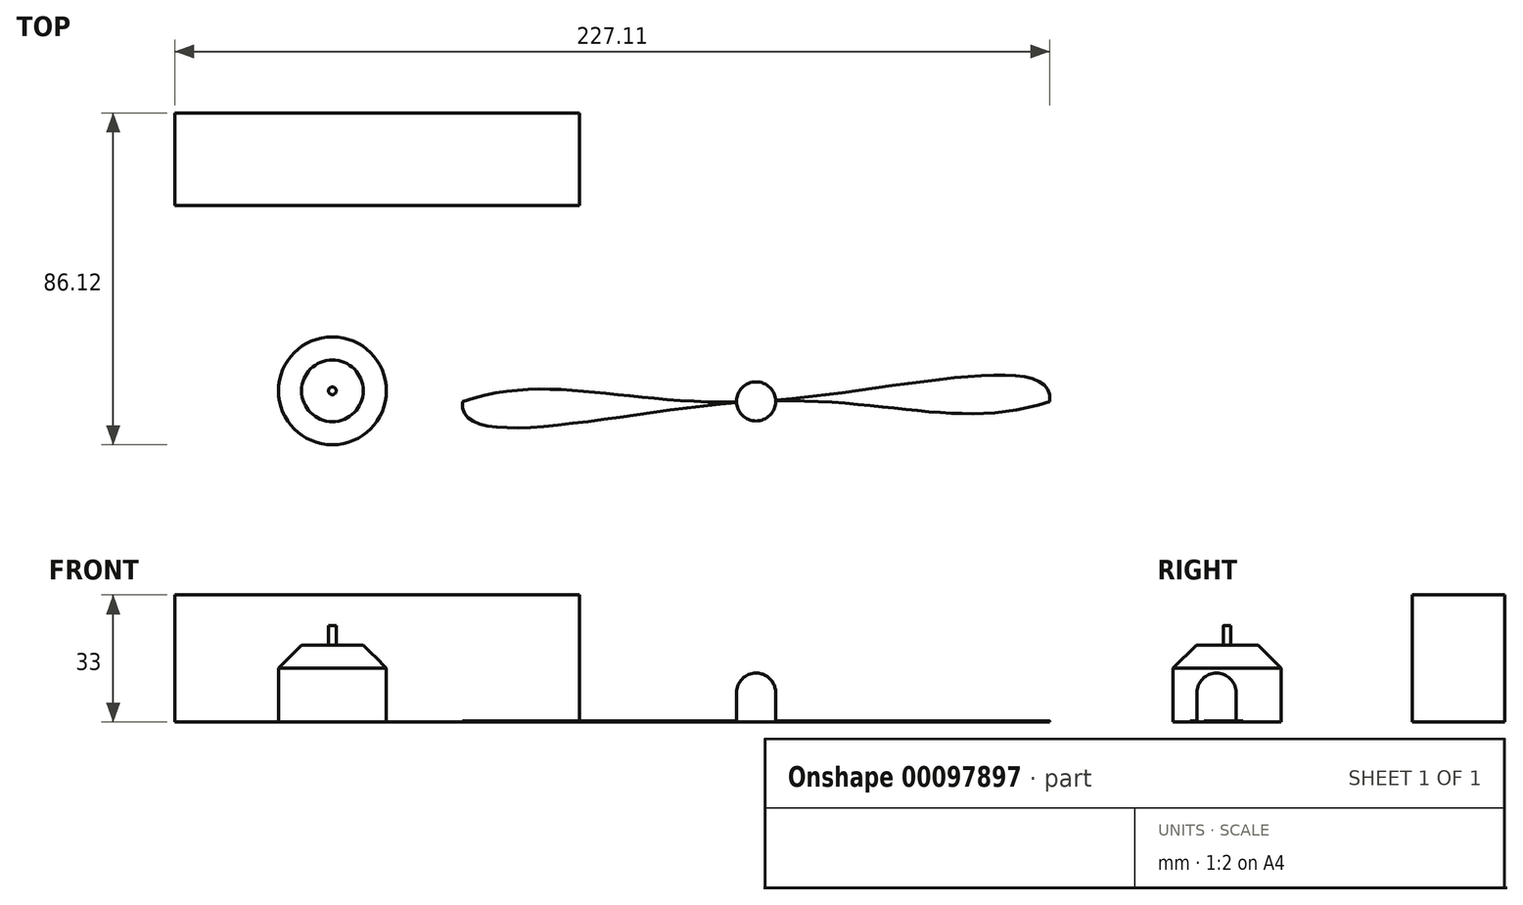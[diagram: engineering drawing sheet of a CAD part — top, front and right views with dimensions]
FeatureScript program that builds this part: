
annotation { "Feature Type Name" : "Feature", "Feature Type Description" : "" }
export const myFeature = defineFeature(function(context is Context, id is Id, definition is map)
    precondition{}
    {
        {
            var Q0;
            Q0=qCreatedBy(makeId("Top.planeOp"),FACE);
            var sketch = newSketch(context, id + "F0", { "sketchPlane" : qUnion([Q0])});
            skLineSegment(sketch, "E0.bottom", {"start": v(-105, 24) * mm, "end": v(0, 24) * mm});
            skLineSegment(sketch, "E0.top", {"start": v(-105, 0) * mm, "end": v(0, 0) * mm});
            skLineSegment(sketch, "E0.left", {"start": v(-105, 24) * mm, "end": v(-105, 0) * mm});
            skLineSegment(sketch, "E0.right", {"start": v(0, 24) * mm, "end": v(0, 0) * mm});
            skSolve(sketch);
        }
        {
            var Q0;
            Q0 = qSketchRegion(id + "F0", true);
            extrude(context, id + "F1", {"entities" : qUnion([Q0]), "depth" : 33 * mm});
        }
        {
            var Q0;
            Q0=qCreatedBy(makeId("Top.planeOp"),FACE);
            var sketch = newSketch(context, id + "F2", { "sketchPlane" : qUnion([Q0])});
            skCircle(sketch, "E1", {"center": v(-64.11, -48.12) * mm, "radius": 14 * mm});
            skSolve(sketch);
        }
        {
            var Q0;
            Q0=makeQuery(id+"F2.imprint","IMPRINT",FACE,{"disambiguationData":[TD([[makeQuery(id+"F2.imprint","IMPRINT",EDGE,{"derivedFrom":sQuery(id+"F2.wireOp",EDGE,"E1")}),1.0]])]});
            var Q1;
            Q1=sQuery(id+"F2.wireOp",EDGE,"E1");
            extrude(context, id + "F3", {"entities" : qUnion([Q0]), "surfaceEntities" : qUnion([Q1]), "depth" : 14 * mm});
        }
        {
            var Q0;
            Q0=makeQuery(id+"F3.opExtrude","CAP_FACE",FACE,{"disambiguationData":[OSD([sQuery(id+"F2.wireOp",EDGE,"E1")])],"isStart":false});
            extrude(context, id + "F4", {"entities" : qUnion([Q0]), "operationType" : NewBodyOperationType.ADD, "depth" : 6 * mm, "hasDraft" : true, "draftAngle" : 45 * degree, "draftPullDirection" : true});
        }
        {
            var Q0;
            Q0=makeQuery(id+"F4.opExtrude","CAP_FACE",FACE,{"disambiguationData":[OSD([sQuery(id+"F2.wireOp",EDGE,"E1")])],"isStart":false});
            var sketch = newSketch(context, id + "F5", { "sketchPlane" : qUnion([Q0])});
            skCircle(sketch, "E2", {"center": v(-64.11, -48.12) * mm, "radius": 1 * mm});
            skSolve(sketch);
        }
        {
            var Q0;
            Q0=makeQuery(id+"F5.imprint","IMPRINT",FACE,{"disambiguationData":[TD([[makeQuery(id+"F5.imprint","IMPRINT",EDGE,{"derivedFrom":sQuery(id+"F5.wireOp",EDGE,"E2")}),1.0]])]});
            extrude(context, id + "F6", {"entities" : qUnion([Q0]), "operationType" : NewBodyOperationType.ADD, "depth" : 5 * mm});
        }
        {
            var Q0;
            Q0=qCreatedBy(makeId("Top.planeOp"),FACE);
            var sketch = newSketch(context, id + "F7", { "sketchPlane" : qUnion([Q0])});
            skCircle(sketch, "E3", {"center": v(45.86, -50.87) * mm, "radius": 5.08 * mm});
            skLineSegment(sketch, "E4", {"start": v(-30.34, -50.87) * mm, "end": v(122.06, -50.87) * mm, "construction": true});
            skFitSpline(sketch, "E5", {"points": [v(-30.34, -50.87) * mm, v(45.86, -50.87) * mm, v(122.06, -50.87) * mm], "startDerivative": vector(141.68, 47.67) * mm, "endDerivative": vector(-10.08, -87.5) * mm});
            skFitSpline(sketch, "E6", {"points": [v(-30.34, -50.87) * mm, v(45.86, -50.87) * mm, v(122.06, -50.87) * mm], "startDerivative": vector(-10.08, -87.5) * mm, "endDerivative": vector(141.68, 47.67) * mm});
            skLineSegment(sketch, "E7", {"start": v(-6.72, -42.93) * mm, "end": v(98.45, -58.81) * mm, "construction": true});
            skLineSegment(sketch, "E8", {"start": v(123.74, -36.29) * mm, "end": v(-32.02, -65.45) * mm, "construction": true});
            skSolve(sketch);
        }
        {
            var Q0;
            {var subQ0=sQuery(id+"F7.wireOp",EDGE,"E5");var subQ1=sQuery(id+"F7.wireOp",EDGE,"E3");var subQ2=makeQuery(id+"F7.imprint","INTERSECT",VERTEX,{"disambiguationData":[OD(0.0)],"derivedFrom":[subQ1,subQ0]});Q0=makeQuery(id+"F7.imprint","IMPRINT",FACE,{"disambiguationData":[TD([[makeQuery(id+"F7.imprint","IMPRINT",EDGE,{"disambiguationData":[TD([[subQ2,1.0]])],"derivedFrom":subQ1}),1.0]])]});}
            var Q1;
            {var subQ0=sQuery(id+"F7.wireOp",EDGE,"E5");var subQ1=sQuery(id+"F7.wireOp",EDGE,"E3");var subQ2=makeQuery(id+"F7.imprint","INTERSECT",VERTEX,{"disambiguationData":[OD(0.0)],"derivedFrom":[subQ1,subQ0]});Q1=makeQuery(id+"F7.imprint","IMPRINT",FACE,{"disambiguationData":[TD([[makeQuery(id+"F7.imprint","IMPRINT",EDGE,{"disambiguationData":[TD([[subQ2,-1.0]])],"derivedFrom":subQ1}),1.0]])]});}
            var Q2;
            {var subQ0=sQuery(id+"F7.wireOp",EDGE,"E6");var subQ1=sQuery(id+"F7.wireOp",EDGE,"E3");var subQ2=makeQuery(id+"F7.imprint","INTERSECT",VERTEX,{"disambiguationData":[OD(0.0)],"derivedFrom":[subQ1,subQ0]});Q2=makeQuery(id+"F7.imprint","IMPRINT",FACE,{"disambiguationData":[TD([[makeQuery(id+"F7.imprint","IMPRINT",EDGE,{"disambiguationData":[TD([[subQ2,1.0]])],"derivedFrom":subQ1}),1.0]])]});}
            var Q3;
            {var subQ0=sQuery(id+"F7.wireOp",EDGE,"E5");var subQ1=sQuery(id+"F7.wireOp",EDGE,"E3");var subQ2=makeQuery(id+"F7.imprint","INTERSECT",VERTEX,{"disambiguationData":[OD(1.0)],"derivedFrom":[subQ1,subQ0]});Q3=makeQuery(id+"F7.imprint","IMPRINT",FACE,{"disambiguationData":[TD([[makeQuery(id+"F7.imprint","IMPRINT",EDGE,{"disambiguationData":[TD([[subQ2,-1.0]])],"derivedFrom":subQ1}),1.0]])]});}
            var Q4;
            Q4=sQuery(id+"F7.wireOp",EDGE,"E3");
            extrude(context, id + "F8", {"entities" : qUnion([Q0, Q1, Q2, Q3]), "surfaceEntities" : qUnion([Q4]), "depth" : 12.7 * mm});
        }
        {
            var Q0;
            {var subQ0=sQuery(id+"F7.wireOp",EDGE,"E5");var subQ1=sQuery(id+"F7.wireOp",EDGE,"E3");var subQ2=makeQuery(id+"F7.imprint","INTERSECT",VERTEX,{"disambiguationData":[OD(1.0)],"derivedFrom":[subQ1,subQ0]});Q0=makeQuery(id+"F7.imprint","IMPRINT",FACE,{"disambiguationData":[TD([[makeQuery(id+"F7.imprint","IMPRINT",EDGE,{"disambiguationData":[TD([[subQ2,-1.0]])],"derivedFrom":subQ1}),-1.0]])]});}
            var Q1;
            {var subQ0=sQuery(id+"F7.wireOp",EDGE,"E5");var subQ1=sQuery(id+"F7.wireOp",EDGE,"E3");var subQ2=makeQuery(id+"F7.imprint","INTERSECT",VERTEX,{"disambiguationData":[OD(0.0)],"derivedFrom":[subQ1,subQ0]});Q1=makeQuery(id+"F7.imprint","IMPRINT",FACE,{"disambiguationData":[TD([[makeQuery(id+"F7.imprint","IMPRINT",EDGE,{"disambiguationData":[TD([[subQ2,1.0]])],"derivedFrom":subQ1}),-1.0]])]});}
            extrude(context, id + "F9", {"entities" : qUnion([Q0, Q1]), "operationType" : NewBodyOperationType.ADD, "depth" : 0.25 * mm});
        }
        {
            var Q0;
            Q0=makeQuery(id+"F8.opExtrude","CAP_EDGE",EDGE,{"disambiguationData":[OSD([sQuery(id+"F7.wireOp",EDGE,"E3")])],"isStart":false});
            fillet(context, id + "F10", {"entities" : qUnion([Q0]), "radius" : 5.08 * mm, "tangentPropagation" : true, "allowEdgeOverflow" : false});
        }
    });
